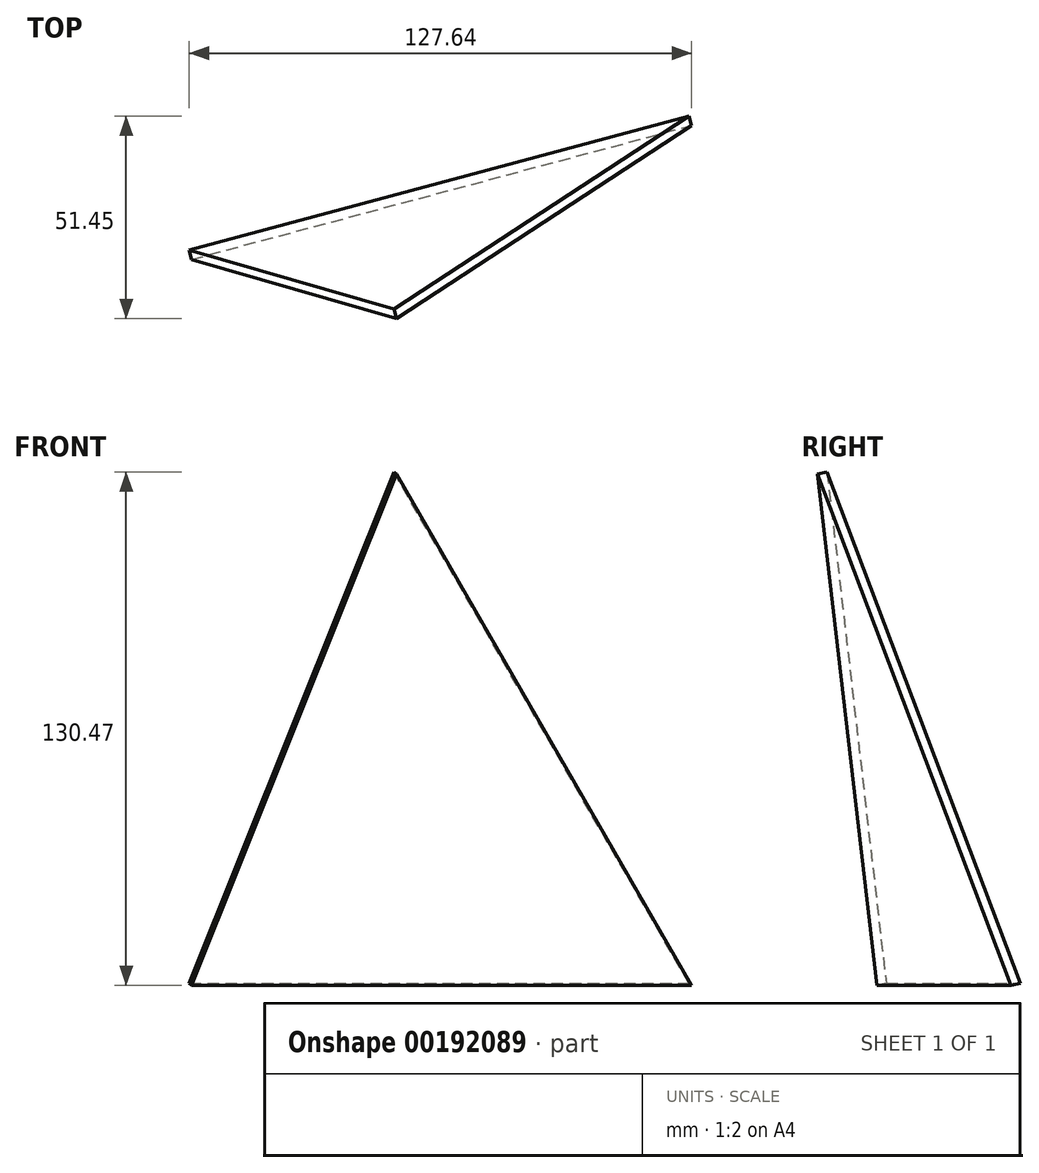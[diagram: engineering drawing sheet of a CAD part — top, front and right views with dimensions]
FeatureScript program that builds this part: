
annotation { "Feature Type Name" : "Feature", "Feature Type Description" : "" }
export const myFeature = defineFeature(function(context is Context, id is Id, definition is map)
    precondition{}
    {
        {
            var Q0;
            Q0=qCreatedBy(makeId("Top.planeOp"),FACE);
            var sketch = newSketch(context, id + "F0", { "sketchPlane" : qUnion([Q0])});
            skCircle(sketch, "E0.cCircle", {"center": v(0, -146.65) * mm, "radius": 73.32 * mm, "construction": true});
            skLineSegment(sketch, "E0.0", {"start": v(0, 0) * mm, "end": v(127, -219.97) * mm, "construction": true});
            skLineSegment(sketch, "E0.1", {"start": v(127, -219.97) * mm, "end": v(-127, -219.97) * mm, "construction": true});
            skLineSegment(sketch, "E0.2", {"start": v(-127, -219.97) * mm, "end": v(0, 0) * mm, "construction": true});
            skPoint(sketch, "E0.0.midPoint", {"position": v(63.5, -109.99) * mm});
            skLineSegment(sketch, "E1", {"start": v(0, 0) * mm, "end": v(-127, 219.97) * mm, "construction": true});
            skLineSegment(sketch, "E2", {"start": v(-127, 219.97) * mm, "end": v(127, 219.97) * mm, "construction": true});
            skLineSegment(sketch, "E3", {"start": v(127, 219.97) * mm, "end": v(0, 0) * mm, "construction": true});
            skArc(sketch, "E4", {"start": v(-127, -219.97) * mm, "mid": v(0, -254) * mm, "end": v(127, -219.97) * mm, "construction": true});
            skArc(sketch, "E5.trimOffspring", {"start": v(127, 219.97) * mm, "mid": v(65.74, 245.35) * mm, "end": v(0, 254) * mm, "construction": true});
            skArc(sketch, "E6", {"start": v(0, 254) * mm, "mid": v(-65.74, 245.35) * mm, "end": v(-127, 219.97) * mm, "construction": true});
            skLineSegment(sketch, "E7", {"start": v(-127, 219.97) * mm, "end": v(0, 254) * mm, "construction": true});
            skLineSegment(sketch, "E8", {"start": v(0, 254) * mm, "end": v(127, 219.97) * mm, "construction": true});
            skSolve(sketch);
        }
        {
            var Q0;
            Q0=qCreatedBy(makeId("Right.planeOp"),FACE);
            var sketch = newSketch(context, id + "F1", { "sketchPlane" : qUnion([Q0])});
            skLineSegment(sketch, "E9", {"start": v(0, 0) * mm, "end": v(-127, -219.97) * mm, "construction": true});
            skLineSegment(sketch, "E10", {"start": v(-127, -219.97) * mm, "end": v(127, -219.97) * mm, "construction": true});
            skLineSegment(sketch, "E11", {"start": v(127, -219.97) * mm, "end": v(0, 0) * mm, "construction": true});
            skLineSegment(sketch, "E12", {"start": v(-127, 219.97) * mm, "end": v(0, 0) * mm, "construction": true});
            skLineSegment(sketch, "E13", {"start": v(127, 219.97) * mm, "end": v(-127, 219.97) * mm, "construction": true});
            skLineSegment(sketch, "E14", {"start": v(0, 0) * mm, "end": v(127, 219.97) * mm, "construction": true});
            skArc(sketch, "E15", {"start": v(127, 219.97) * mm, "mid": v(0, 254) * mm, "end": v(-127, 219.97) * mm, "construction": true});
            skArc(sketch, "E16.trimOffspring", {"start": v(-127, -219.97) * mm, "mid": v(0, -254) * mm, "end": v(127, -219.97) * mm, "construction": true});
            skLineSegment(sketch, "E17", {"start": v(127, 219.97) * mm, "end": v(0, 254) * mm, "construction": true});
            skLineSegment(sketch, "E18", {"start": v(0, 254) * mm, "end": v(-127, 219.97) * mm, "construction": true});
            skLineSegment(sketch, "E19", {"start": v(127, -219.97) * mm, "end": v(0, -254) * mm, "construction": true});
            skLineSegment(sketch, "E20", {"start": v(0, -254) * mm, "end": v(-127, -219.97) * mm, "construction": true});
            skSolve(sketch);
        }
        {
            var Q0;
            Q0=qCreatedBy(makeId("Front.planeOp"),FACE);
            var sketch = newSketch(context, id + "F2", { "sketchPlane" : qUnion([Q0])});
            skLineSegment(sketch, "E21", {"start": v(-219.97, -127) * mm, "end": v(0, 0) * mm, "construction": true});
            skLineSegment(sketch, "E22", {"start": v(219.97, 127) * mm, "end": v(219.97, -127) * mm, "construction": true});
            skLineSegment(sketch, "E23", {"start": v(219.97, -127) * mm, "end": v(0, 0) * mm, "construction": true});
            skLineSegment(sketch, "E24", {"start": v(-219.97, 127) * mm, "end": v(-219.97, -127) * mm, "construction": true});
            skLineSegment(sketch, "E25", {"start": v(0, 0) * mm, "end": v(219.97, 127) * mm, "construction": true});
            skLineSegment(sketch, "E26", {"start": v(0, 0) * mm, "end": v(-219.97, 127) * mm, "construction": true});
            skArc(sketch, "E27", {"start": v(-219.97, 127) * mm, "mid": v(-254, 0) * mm, "end": v(-219.97, -127) * mm, "construction": true});
            skArc(sketch, "E28.trimOffspring", {"start": v(219.97, -127) * mm, "mid": v(254, 0) * mm, "end": v(219.97, 127) * mm, "construction": true});
            skArc(sketch, "E29", {"start": v(-219.97, 127) * mm, "mid": v(0, 254) * mm, "end": v(219.97, 127) * mm, "construction": true});
            skArc(sketch, "E30", {"start": v(-219.97, -127) * mm, "mid": v(0, -254) * mm, "end": v(219.97, -127) * mm, "construction": true});
            skLineSegment(sketch, "E31", {"start": v(219.97, 127) * mm, "end": v(254, 0) * mm, "construction": true});
            skLineSegment(sketch, "E32", {"start": v(254, 0) * mm, "end": v(219.97, -127) * mm, "construction": true});
            skLineSegment(sketch, "E33", {"start": v(-219.97, 127) * mm, "end": v(-254, 0) * mm, "construction": true});
            skLineSegment(sketch, "E34", {"start": v(-254, 0) * mm, "end": v(-219.97, -127) * mm, "construction": true});
            skSolve(sketch);
        }
        {
            var Q0;
            Q0=sQuery(id+"F0.wireOp",VERTEX,"E3.start");
            var Q1;
            Q1=sQuery(id+"F2.wireOp",VERTEX,"E23.start");
            var Q2;
            Q2=sQuery(id+"F1.wireOp",VERTEX,"E11.start");
            cPlane(context, id + "F3", {"entities" : qUnion([Q0, Q1, Q2]), "cplaneType" : CPlaneType.THREE_POINT, "offset" : 25.4 * mm, "width" : 152.4 * mm, "height" : 152.4 * mm});
        }
        {
            var Q0;
            Q0=sQuery(id+"F1.wireOp",VERTEX,"E14.end");
            var Q1;
            Q1=sQuery(id+"F0.wireOp",VERTEX,"E3.start");
            var Q2;
            Q2=sQuery(id+"F2.wireOp",VERTEX,"E25.end");
            cPlane(context, id + "F4", {"entities" : qUnion([Q0, Q1, Q2]), "cplaneType" : CPlaneType.THREE_POINT, "offset" : 25.4 * mm, "width" : 152.4 * mm, "height" : 152.4 * mm});
        }
        {
            var Q0;
            Q0=sQuery(id+"F1.wireOp",VERTEX,"E14.end");
            var Q1;
            Q1=sQuery(id+"F0.wireOp",VERTEX,"E2.start");
            var Q2;
            Q2=sQuery(id+"F2.wireOp",VERTEX,"E26.end");
            cPlane(context, id + "F5", {"entities" : qUnion([Q0, Q1, Q2]), "cplaneType" : CPlaneType.THREE_POINT, "offset" : 25.4 * mm, "width" : 152.4 * mm, "height" : 152.4 * mm});
        }
        {
            var Q0;
            Q0=sQuery(id+"F0.wireOp",VERTEX,"E2.start");
            var Q1;
            Q1=sQuery(id+"F2.wireOp",VERTEX,"E24.end");
            var Q2;
            Q2=sQuery(id+"F1.wireOp",VERTEX,"E11.start");
            cPlane(context, id + "F6", {"entities" : qUnion([Q0, Q1, Q2]), "cplaneType" : CPlaneType.THREE_POINT, "offset" : 25.4 * mm, "width" : 152.4 * mm, "height" : 152.4 * mm});
        }
        {
            var Q0;
            Q0=qCreatedBy(id+"F4.planeOp",FACE);
            var sketch = newSketch(context, id + "F7", { "sketchPlane" : qUnion([Q0])});
            skLineSegment(sketch, "E35", {"start": v(13.9, 155.54) * mm, "end": v(127.76, -89.8) * mm, "construction": true});
            skLineSegment(sketch, "E36", {"start": v(127.76, -89.8) * mm, "end": v(-141.65, -65.74) * mm, "construction": true});
            skLineSegment(sketch, "E37", {"start": v(-141.65, -65.74) * mm, "end": v(13.9, 155.54) * mm, "construction": true});
            skSolve(sketch);
        }
        {
            var Q0;
            Q0=qCreatedBy(id+"F5.planeOp",FACE);
            var sketch = newSketch(context, id + "F8", { "sketchPlane" : qUnion([Q0])});
            skLineSegment(sketch, "E38", {"start": v(-13.9, -155.54) * mm, "end": v(141.65, 65.74) * mm, "construction": true});
            skLineSegment(sketch, "E39", {"start": v(141.65, 65.74) * mm, "end": v(-127.76, 89.8) * mm, "construction": true});
            skLineSegment(sketch, "E40", {"start": v(-127.76, 89.8) * mm, "end": v(-13.9, -155.54) * mm, "construction": true});
            skSolve(sketch);
        }
        {
            var Q0;
            Q0=sQuery(id+"F1.wireOp",VERTEX,"E11.start");
            var Q1;
            Q1=sQuery(id+"F0.wireOp",VERTEX,"E2.start");
            var Q2;
            Q2=qCreatedBy(makeId("Origin.pointOp"),VERTEX);
            cPlane(context, id + "F9", {"entities" : qUnion([Q0, Q1, Q2]), "cplaneType" : CPlaneType.THREE_POINT, "offset" : 25.4 * mm, "width" : 152.4 * mm, "height" : 152.4 * mm});
        }
        {
            var Q0;
            Q0=sQuery(id+"F1.wireOp",VERTEX,"E11.start");
            var Q1;
            Q1=sQuery(id+"F2.wireOp",VERTEX,"E24.end");
            var Q2;
            Q2=qCreatedBy(makeId("Origin.pointOp"),VERTEX);
            cPlane(context, id + "F10", {"entities" : qUnion([Q0, Q1, Q2]), "cplaneType" : CPlaneType.THREE_POINT, "offset" : 25.4 * mm, "width" : 152.4 * mm, "height" : 152.4 * mm});
        }
        {
            var Q0;
            Q0=sQuery(id+"F2.wireOp",VERTEX,"E24.end");
            var Q1;
            Q1=sQuery(id+"F0.wireOp",VERTEX,"E2.start");
            var Q2;
            Q2=qCreatedBy(makeId("Origin.pointOp"),VERTEX);
            cPlane(context, id + "F11", {"entities" : qUnion([Q0, Q1, Q2]), "cplaneType" : CPlaneType.THREE_POINT, "offset" : 25.4 * mm, "width" : 152.4 * mm, "height" : 152.4 * mm});
        }
        {
            var Q0;
            Q0=qCreatedBy(id+"F9.planeOp",FACE);
            var sketch = newSketch(context, id + "F12", { "sketchPlane" : qUnion([Q0])});
            skLineSegment(sketch, "E41.0", {"start": v(0, 0) * mm, "end": v(-250.8, 40.16) * mm, "construction": true});
            skLineSegment(sketch, "E42.0", {"start": v(-144.8, -208.68) * mm, "end": v(0, 0) * mm, "construction": true});
            skLineSegment(sketch, "E43", {"start": v(-250.8, 40.16) * mm, "end": v(-144.8, -208.68) * mm, "construction": true});
            skArc(sketch, "E44.trimOffspring", {"start": v(-250.8, 40.16) * mm, "mid": v(-233.68, -99.54) * mm, "end": v(-144.8, -208.68) * mm, "construction": true});
            skLineSegment(sketch, "E45", {"start": v(-144.8, -208.68) * mm, "end": v(-233.68, -99.54) * mm, "construction": true});
            skLineSegment(sketch, "E46", {"start": v(-233.68, -99.54) * mm, "end": v(-250.8, 40.16) * mm, "construction": true});
            skSolve(sketch);
        }
        {
            var Q0;
            Q0=qCreatedBy(id+"F10.planeOp",FACE);
            var sketch = newSketch(context, id + "F13", { "sketchPlane" : qUnion([Q0])});
            skArc(sketch, "E47", {"start": v(-228.95, -109.99) * mm, "mid": v(-135.24, -215) * mm, "end": v(0, -254) * mm, "construction": true});
            skLineSegment(sketch, "E48.0", {"start": v(-228.95, -109.99) * mm, "end": v(0, 0) * mm, "construction": true});
            skLineSegment(sketch, "E48.1", {"start": v(0, -254) * mm, "end": v(0, 0) * mm, "construction": true});
            skLineSegment(sketch, "E49", {"start": v(-228.95, -109.99) * mm, "end": v(0, -254) * mm, "construction": true});
            skLineSegment(sketch, "E50", {"start": v(-228.95, -109.99) * mm, "end": v(-135.24, -215) * mm, "construction": true});
            skLineSegment(sketch, "E51", {"start": v(-135.24, -215) * mm, "end": v(0, -254) * mm, "construction": true});
            skSolve(sketch);
        }
        {
            var Q0;
            Q0=qCreatedBy(id+"F11.planeOp",FACE);
            var sketch = newSketch(context, id + "F14", { "sketchPlane" : qUnion([Q0])});
            skArc(sketch, "E52", {"start": v(-144.8, 208.68) * mm, "mid": v(-233.68, 99.54) * mm, "end": v(-250.8, -40.16) * mm, "construction": true});
            skLineSegment(sketch, "E53.1", {"start": v(0, 0) * mm, "end": v(-144.8, 208.68) * mm, "construction": true});
            skLineSegment(sketch, "E53.2", {"start": v(-250.8, -40.16) * mm, "end": v(0, 0) * mm, "construction": true});
            skLineSegment(sketch, "E54", {"start": v(-144.8, 208.68) * mm, "end": v(-250.8, -40.16) * mm, "construction": true});
            skLineSegment(sketch, "E55", {"start": v(-250.8, -40.16) * mm, "end": v(-233.68, 99.54) * mm, "construction": true});
            skLineSegment(sketch, "E56", {"start": v(-233.68, 99.54) * mm, "end": v(-144.8, 208.68) * mm, "construction": true});
            skSolve(sketch);
        }
        {
            var Q0;
            Q0=sQuery(id+"F2.wireOp",VERTEX,"E30.end");
            var Q1;
            Q1=qCreatedBy(makeId("Origin.pointOp"),VERTEX);
            var Q2;
            Q2=sQuery(id+"F1.wireOp",VERTEX,"E11.start");
            cPlane(context, id + "F15", {"entities" : qUnion([Q0, Q1, Q2]), "cplaneType" : CPlaneType.THREE_POINT, "offset" : 25.4 * mm, "width" : 152.4 * mm, "height" : 152.4 * mm});
        }
        {
            var Q0;
            Q0=qCreatedBy(makeId("Origin.pointOp"),VERTEX);
            var Q1;
            Q1=sQuery(id+"F2.wireOp",VERTEX,"E30.end");
            var Q2;
            Q2=sQuery(id+"F0.wireOp",VERTEX,"E3.start");
            cPlane(context, id + "F16", {"entities" : qUnion([Q0, Q1, Q2]), "cplaneType" : CPlaneType.THREE_POINT, "offset" : 25.4 * mm, "width" : 152.4 * mm, "height" : 152.4 * mm});
        }
        {
            var Q0;
            Q0=qCreatedBy(makeId("Origin.pointOp"),VERTEX);
            var Q1;
            Q1=sQuery(id+"F0.wireOp",VERTEX,"E3.start");
            var Q2;
            Q2=sQuery(id+"F1.wireOp",VERTEX,"E11.start");
            cPlane(context, id + "F17", {"entities" : qUnion([Q0, Q1, Q2]), "cplaneType" : CPlaneType.THREE_POINT, "offset" : 25.4 * mm, "width" : 152.4 * mm, "height" : 152.4 * mm});
        }
        {
            var Q0;
            Q0=qCreatedBy(makeId("Origin.pointOp"),VERTEX);
            var Q1;
            Q1=sQuery(id+"F0.wireOp",VERTEX,"E3.start");
            var Q2;
            Q2=sQuery(id+"F2.wireOp",VERTEX,"E25.end");
            cPlane(context, id + "F18", {"entities" : qUnion([Q0, Q1, Q2]), "cplaneType" : CPlaneType.THREE_POINT, "offset" : 25.4 * mm, "width" : 152.4 * mm, "height" : 152.4 * mm});
        }
        {
            var Q0;
            Q0=qCreatedBy(makeId("Origin.pointOp"),VERTEX);
            var Q1;
            Q1=sQuery(id+"F2.wireOp",VERTEX,"E25.end");
            var Q2;
            Q2=sQuery(id+"F1.wireOp",VERTEX,"E15.start");
            cPlane(context, id + "F19", {"entities" : qUnion([Q0, Q1, Q2]), "cplaneType" : CPlaneType.THREE_POINT, "offset" : 25.4 * mm, "width" : 152.4 * mm, "height" : 152.4 * mm});
        }
        {
            var Q0;
            Q0=qCreatedBy(makeId("Origin.pointOp"),VERTEX);
            var Q1;
            Q1=sQuery(id+"F1.wireOp",VERTEX,"E15.start");
            var Q2;
            Q2=sQuery(id+"F0.wireOp",VERTEX,"E3.start");
            cPlane(context, id + "F20", {"entities" : qUnion([Q0, Q1, Q2]), "cplaneType" : CPlaneType.THREE_POINT, "offset" : 25.4 * mm, "width" : 152.4 * mm, "height" : 152.4 * mm});
        }
        {
            var Q0;
            Q0=qCreatedBy(makeId("Origin.pointOp"),VERTEX);
            var Q1;
            Q1=sQuery(id+"F0.wireOp",VERTEX,"E2.start");
            var Q2;
            Q2=sQuery(id+"F2.wireOp",VERTEX,"E27.start");
            cPlane(context, id + "F21", {"entities" : qUnion([Q0, Q1, Q2]), "cplaneType" : CPlaneType.THREE_POINT, "offset" : 25.4 * mm, "width" : 152.4 * mm, "height" : 152.4 * mm});
        }
        {
            var Q0;
            Q0=qCreatedBy(makeId("Origin.pointOp"),VERTEX);
            var Q1;
            Q1=sQuery(id+"F0.wireOp",VERTEX,"E2.start");
            var Q2;
            Q2=sQuery(id+"F1.wireOp",VERTEX,"E15.start");
            cPlane(context, id + "F22", {"entities" : qUnion([Q0, Q1, Q2]), "cplaneType" : CPlaneType.THREE_POINT, "offset" : 25.4 * mm, "width" : 152.4 * mm, "height" : 152.4 * mm});
        }
        {
            var Q0;
            Q0=qCreatedBy(makeId("Origin.pointOp"),VERTEX);
            var Q1;
            Q1=sQuery(id+"F2.wireOp",VERTEX,"E27.start");
            var Q2;
            Q2=sQuery(id+"F1.wireOp",VERTEX,"E15.start");
            cPlane(context, id + "F23", {"entities" : qUnion([Q0, Q1, Q2]), "cplaneType" : CPlaneType.THREE_POINT, "offset" : 25.4 * mm, "width" : 152.4 * mm, "height" : 152.4 * mm});
        }
        {
            var Q0;
            Q0=qCreatedBy(id+"F15.planeOp",FACE);
            var sketch = newSketch(context, id + "F24", { "sketchPlane" : qUnion([Q0])});
            skArc(sketch, "E57", {"start": v(-228.95, -109.99) * mm, "mid": v(-135.24, -215) * mm, "end": v(0, -254) * mm, "construction": true});
            skLineSegment(sketch, "E58.0", {"start": v(-228.95, -109.99) * mm, "end": v(0, 0) * mm, "construction": true});
            skLineSegment(sketch, "E58.1", {"start": v(0, -254) * mm, "end": v(0, 0) * mm, "construction": true});
            skLineSegment(sketch, "E59", {"start": v(0, -254) * mm, "end": v(-228.95, -109.99) * mm, "construction": true});
            skLineSegment(sketch, "E60", {"start": v(-228.95, -109.99) * mm, "end": v(-135.24, -215) * mm, "construction": true});
            skLineSegment(sketch, "E61", {"start": v(-135.24, -215) * mm, "end": v(0, -254) * mm, "construction": true});
            skSolve(sketch);
        }
        {
            var Q0;
            Q0=qCreatedBy(id+"F16.planeOp",FACE);
            var sketch = newSketch(context, id + "F25", { "sketchPlane" : qUnion([Q0])});
            skArc(sketch, "E62", {"start": v(144.8, -208.68) * mm, "mid": v(233.68, -99.54) * mm, "end": v(250.8, 40.16) * mm, "construction": true});
            skLineSegment(sketch, "E63.0", {"start": v(144.8, -208.68) * mm, "end": v(0, 0) * mm, "construction": true});
            skLineSegment(sketch, "E63.1", {"start": v(250.8, 40.16) * mm, "end": v(0, 0) * mm, "construction": true});
            skLineSegment(sketch, "E64", {"start": v(144.8, -208.68) * mm, "end": v(250.8, 40.16) * mm, "construction": true});
            skLineSegment(sketch, "E65", {"start": v(144.8, -208.68) * mm, "end": v(233.68, -99.54) * mm, "construction": true});
            skLineSegment(sketch, "E66", {"start": v(233.68, -99.54) * mm, "end": v(250.8, 40.16) * mm, "construction": true});
            skSolve(sketch);
        }
        {
            var Q0;
            Q0=qCreatedBy(id+"F17.planeOp",FACE);
            var sketch = newSketch(context, id + "F26", { "sketchPlane" : qUnion([Q0])});
            skArc(sketch, "E67", {"start": v(144.8, -208.68) * mm, "mid": v(233.68, -99.54) * mm, "end": v(250.8, 40.16) * mm, "construction": true});
            skLineSegment(sketch, "E68.0", {"start": v(250.8, 40.16) * mm, "end": v(0, 0) * mm, "construction": true});
            skLineSegment(sketch, "E68.1", {"start": v(144.8, -208.68) * mm, "end": v(0, 0) * mm, "construction": true});
            skLineSegment(sketch, "E69", {"start": v(250.8, 40.16) * mm, "end": v(144.8, -208.68) * mm, "construction": true});
            skLineSegment(sketch, "E70", {"start": v(250.8, 40.16) * mm, "end": v(233.68, -99.54) * mm, "construction": true});
            skLineSegment(sketch, "E71", {"start": v(233.68, -99.54) * mm, "end": v(144.8, -208.68) * mm, "construction": true});
            skSolve(sketch);
        }
        {
            var Q0;
            Q0=qCreatedBy(id+"F18.planeOp",FACE);
            var sketch = newSketch(context, id + "F27", { "sketchPlane" : qUnion([Q0])});
            skArc(sketch, "E72", {"start": v(250.8, -40.16) * mm, "mid": v(233.68, 99.54) * mm, "end": v(144.8, 208.68) * mm, "construction": true});
            skLineSegment(sketch, "E73.0", {"start": v(144.8, 208.68) * mm, "end": v(0, 0) * mm, "construction": true});
            skLineSegment(sketch, "E73.1", {"start": v(0, 0) * mm, "end": v(250.8, -40.16) * mm, "construction": true});
            skLineSegment(sketch, "E74", {"start": v(144.8, 208.68) * mm, "end": v(250.8, -40.16) * mm, "construction": true});
            skLineSegment(sketch, "E75", {"start": v(144.8, 208.68) * mm, "end": v(233.68, 99.54) * mm, "construction": true});
            skLineSegment(sketch, "E76", {"start": v(233.68, 99.54) * mm, "end": v(250.8, -40.16) * mm, "construction": true});
            skSolve(sketch);
        }
        {
            var Q0;
            Q0=qCreatedBy(id+"F19.planeOp",FACE);
            var sketch = newSketch(context, id + "F28", { "sketchPlane" : qUnion([Q0])});
            skArc(sketch, "E77", {"start": v(0, 254) * mm, "mid": v(-135.24, 215) * mm, "end": v(-228.95, 109.99) * mm, "construction": true});
            skLineSegment(sketch, "E78.0", {"start": v(0, 0) * mm, "end": v(0, 254) * mm, "construction": true});
            skLineSegment(sketch, "E78.1", {"start": v(0, 0) * mm, "end": v(-228.95, 109.99) * mm, "construction": true});
            skLineSegment(sketch, "E79", {"start": v(0, 254) * mm, "end": v(-228.95, 109.99) * mm, "construction": true});
            skLineSegment(sketch, "E80", {"start": v(0, 254) * mm, "end": v(-135.24, 215) * mm, "construction": true});
            skLineSegment(sketch, "E81", {"start": v(-135.24, 215) * mm, "end": v(-228.95, 109.99) * mm, "construction": true});
            skSolve(sketch);
        }
        {
            var Q0;
            Q0=qCreatedBy(id+"F20.planeOp",FACE);
            var sketch = newSketch(context, id + "F29", { "sketchPlane" : qUnion([Q0])});
            skArc(sketch, "E82", {"start": v(250.8, -40.16) * mm, "mid": v(233.68, 99.54) * mm, "end": v(144.8, 208.68) * mm, "construction": true});
            skLineSegment(sketch, "E83.0", {"start": v(250.8, -40.16) * mm, "end": v(0, 0) * mm, "construction": true});
            skLineSegment(sketch, "E83.1", {"start": v(0, 0) * mm, "end": v(144.8, 208.68) * mm, "construction": true});
            skLineSegment(sketch, "E84", {"start": v(250.8, -40.16) * mm, "end": v(144.8, 208.68) * mm, "construction": true});
            skLineSegment(sketch, "E85", {"start": v(144.8, 208.68) * mm, "end": v(233.68, 99.54) * mm, "construction": true});
            skLineSegment(sketch, "E86", {"start": v(233.68, 99.54) * mm, "end": v(250.8, -40.16) * mm, "construction": true});
            skSolve(sketch);
        }
        {
            var Q0;
            Q0=qCreatedBy(id+"F21.planeOp",FACE);
            var sketch = newSketch(context, id + "F30", { "sketchPlane" : qUnion([Q0])});
            skArc(sketch, "E87", {"start": v(-250.8, 40.16) * mm, "mid": v(-233.68, -99.54) * mm, "end": v(-144.8, -208.68) * mm, "construction": true});
            skLineSegment(sketch, "E88.0", {"start": v(0, 0) * mm, "end": v(-144.8, -208.68) * mm, "construction": true});
            skLineSegment(sketch, "E88.1", {"start": v(0, 0) * mm, "end": v(-250.8, 40.16) * mm, "construction": true});
            skLineSegment(sketch, "E89", {"start": v(-144.8, -208.68) * mm, "end": v(-250.8, 40.16) * mm, "construction": true});
            skLineSegment(sketch, "E90", {"start": v(-250.8, 40.16) * mm, "end": v(-233.68, -99.54) * mm, "construction": true});
            skLineSegment(sketch, "E91", {"start": v(-233.68, -99.54) * mm, "end": v(-144.8, -208.68) * mm, "construction": true});
            skSolve(sketch);
        }
        {
            var Q0;
            Q0=qCreatedBy(id+"F22.planeOp",FACE);
            var sketch = newSketch(context, id + "F31", { "sketchPlane" : qUnion([Q0])});
            skArc(sketch, "E92", {"start": v(-144.8, 208.68) * mm, "mid": v(-233.68, 99.54) * mm, "end": v(-250.8, -40.16) * mm, "construction": true});
            skLineSegment(sketch, "E93.1", {"start": v(0, 0) * mm, "end": v(-250.8, -40.16) * mm, "construction": true});
            skLineSegment(sketch, "E93.2", {"start": v(0, 0) * mm, "end": v(-144.8, 208.68) * mm, "construction": true});
            skLineSegment(sketch, "E94", {"start": v(-250.8, -40.16) * mm, "end": v(-144.8, 208.68) * mm, "construction": true});
            skLineSegment(sketch, "E95", {"start": v(-144.8, 208.68) * mm, "end": v(-233.68, 99.54) * mm, "construction": true});
            skLineSegment(sketch, "E96", {"start": v(-233.68, 99.54) * mm, "end": v(-250.8, -40.16) * mm, "construction": true});
            skSolve(sketch);
        }
        {
            var Q0;
            Q0=qCreatedBy(id+"F23.planeOp",FACE);
            var sketch = newSketch(context, id + "F32", { "sketchPlane" : qUnion([Q0])});
            skArc(sketch, "E97", {"start": v(0, 254) * mm, "mid": v(-135.24, 215) * mm, "end": v(-228.95, 109.99) * mm, "construction": true});
            skLineSegment(sketch, "E98.0", {"start": v(0, 0) * mm, "end": v(-228.95, 109.99) * mm, "construction": true});
            skLineSegment(sketch, "E98.1", {"start": v(0, 0) * mm, "end": v(0, 254) * mm, "construction": true});
            skLineSegment(sketch, "E99", {"start": v(-228.95, 109.99) * mm, "end": v(0, 254) * mm, "construction": true});
            skLineSegment(sketch, "E100", {"start": v(0, 254) * mm, "end": v(-135.24, 215) * mm, "construction": true});
            skLineSegment(sketch, "E101", {"start": v(-135.24, 215) * mm, "end": v(-228.95, 109.99) * mm, "construction": true});
            skSolve(sketch);
        }
        {
            var Q0;
            Q0=sQuery(id+"F0.wireOp",VERTEX,"E5.trimOffspring.end");
            var Q1;
            Q1=sQuery(id+"F26.wireOp",VERTEX,"E71.start");
            var Q2;
            Q2=sQuery(id+"F12.wireOp",VERTEX,"E46.start");
            cPlane(context, id + "F33", {"entities" : qUnion([Q0, Q1, Q2]), "cplaneType" : CPlaneType.THREE_POINT, "offset" : 25.4 * mm, "width" : 152.4 * mm, "height" : 152.4 * mm});
        }
        {
            var Q0;
            Q0=sQuery(id+"F31.wireOp",VERTEX,"E96.start");
            var Q1;
            Q1=sQuery(id+"F0.wireOp",VERTEX,"E6.start");
            var Q2;
            Q2=sQuery(id+"F29.wireOp",VERTEX,"E86.start");
            cPlane(context, id + "F34", {"entities" : qUnion([Q0, Q1, Q2]), "cplaneType" : CPlaneType.THREE_POINT, "offset" : 25.4 * mm, "width" : 152.4 * mm, "height" : 152.4 * mm});
        }
        {
            var Q0;
            Q0=sQuery(id+"F31.wireOp",VERTEX,"E96.start");
            var Q1;
            Q1=sQuery(id+"F30.wireOp",VERTEX,"E91.start");
            var Q2;
            Q2=sQuery(id+"F32.wireOp",VERTEX,"E101.start");
            cPlane(context, id + "F35", {"entities" : qUnion([Q0, Q1, Q2]), "cplaneType" : CPlaneType.THREE_POINT, "offset" : 25.4 * mm, "width" : 152.4 * mm, "height" : 152.4 * mm});
        }
        {
            var Q0;
            Q0=sQuery(id+"F14.wireOp",VERTEX,"E56.start");
            var Q1;
            Q1=sQuery(id+"F12.wireOp",VERTEX,"E46.start");
            var Q2;
            Q2=sQuery(id+"F13.wireOp",VERTEX,"E51.start");
            cPlane(context, id + "F36", {"entities" : qUnion([Q0, Q1, Q2]), "cplaneType" : CPlaneType.THREE_POINT, "offset" : 25.4 * mm, "width" : 152.4 * mm, "height" : 152.4 * mm});
        }
        {
            var Q0;
            Q0=sQuery(id+"F26.wireOp",VERTEX,"E71.start");
            var Q1;
            Q1=sQuery(id+"F25.wireOp",VERTEX,"E66.start");
            var Q2;
            Q2=sQuery(id+"F24.wireOp",VERTEX,"E61.start");
            cPlane(context, id + "F37", {"entities" : qUnion([Q0, Q1, Q2]), "cplaneType" : CPlaneType.THREE_POINT, "offset" : 25.4 * mm, "width" : 152.4 * mm, "height" : 152.4 * mm});
        }
        {
            var Q0;
            Q0=sQuery(id+"F28.wireOp",EDGE,"E77");
            cPoint(context, id + "F38", {"entities" : qUnion([Q0]), "parameter" : 0.5});
        }
        {
            var Q0;
            Q0=sQuery(id+"F27.wireOp",EDGE,"E72");
            cPoint(context, id + "F39", {"entities" : qUnion([Q0]), "parameter" : 0.5});
        }
        {
            var Q0;
            Q0=sQuery(id+"F29.wireOp",VERTEX,"E86.start");
            var Q1;
            Q1 = qCreatedBy(id + "F38" ,VERTEX);
            var Q2;
            Q2 = qCreatedBy(id + "F39" ,VERTEX);
            cPlane(context, id + "F40", {"entities" : qUnion([Q0, Q1, Q2]), "cplaneType" : CPlaneType.THREE_POINT, "offset" : 25.4 * mm, "width" : 152.4 * mm, "height" : 152.4 * mm});
        }
        {
            var Q0;
            Q0=sQuery(id+"F2.wireOp",VERTEX,"E32.start");
            var Q1;
            Q1=sQuery(id+"F27.wireOp",VERTEX,"E76.start");
            var Q2;
            Q2=sQuery(id+"F25.wireOp",VERTEX,"E66.start");
            cPlane(context, id + "F41", {"entities" : qUnion([Q0, Q1, Q2]), "cplaneType" : CPlaneType.THREE_POINT, "offset" : 25.4 * mm, "width" : 152.4 * mm, "height" : 152.4 * mm});
        }
        {
            var Q0;
            Q0=sQuery(id+"F30.wireOp",EDGE,"E87");
            cPoint(context, id + "F42", {"entities" : qUnion([Q0]), "parameter" : 0.5});
        }
        {
            var Q0;
            Q0=sQuery(id+"F14.wireOp",VERTEX,"E56.start");
            var Q1;
            Q1 = qCreatedBy(id + "F42" ,VERTEX);
            var Q2;
            Q2=sQuery(id+"F2.wireOp",VERTEX,"E34.start");
            cPlane(context, id + "F43", {"entities" : qUnion([Q0, Q1, Q2]), "cplaneType" : CPlaneType.THREE_POINT, "offset" : 25.4 * mm, "width" : 152.4 * mm, "height" : 152.4 * mm});
        }
        {
            var Q0;
            Q0=qCreatedBy(id+"F33.planeOp",FACE);
            var sketch = newSketch(context, id + "F44", { "sketchPlane" : qUnion([Q0])});
            skPoint(sketch, "E102.0", {"position": v(-75.02, -49.18) * mm});
            skPoint(sketch, "E102.1", {"position": v(75.02, -49.18) * mm});
            skPoint(sketch, "E102.2", {"position": v(0, 89.7) * mm});
            skLineSegment(sketch, "E103", {"start": v(-75.02, -49.18) * mm, "end": v(0, 89.7) * mm, "construction": true});
            skLineSegment(sketch, "E104", {"start": v(75.02, -49.18) * mm, "end": v(-75.02, -49.18) * mm, "construction": true});
            skLineSegment(sketch, "E105", {"start": v(75.02, -49.18) * mm, "end": v(0, 89.7) * mm, "construction": true});
            skSolve(sketch);
        }
        {
            var Q0;
            Q0=qCreatedBy(id+"F34.planeOp",FACE);
            var sketch = newSketch(context, id + "F45", { "sketchPlane" : qUnion([Q0])});
            skPoint(sketch, "E106.0", {"position": v(-75.02, 49.18) * mm});
            skPoint(sketch, "E106.1", {"position": v(0, -89.7) * mm});
            skPoint(sketch, "E106.2", {"position": v(75.02, 49.18) * mm});
            skLineSegment(sketch, "E107", {"start": v(-75.02, 49.18) * mm, "end": v(75.02, 49.18) * mm, "construction": true});
            skLineSegment(sketch, "E108", {"start": v(0, -89.7) * mm, "end": v(-75.02, 49.18) * mm, "construction": true});
            skLineSegment(sketch, "E109", {"start": v(0, -89.7) * mm, "end": v(75.02, 49.18) * mm, "construction": true});
            skSolve(sketch);
        }
        {
            var Q0;
            Q0=qCreatedBy(id+"F35.planeOp",FACE);
            var sketch = newSketch(context, id + "F46", { "sketchPlane" : qUnion([Q0])});
            skPoint(sketch, "E110.0", {"position": v(83.67, 38.83) * mm});
            skPoint(sketch, "E110.1", {"position": v(-75.47, 53.05) * mm});
            skPoint(sketch, "E110.2", {"position": v(-8.2, -91.88) * mm});
            skLineSegment(sketch, "E111", {"start": v(83.67, 38.83) * mm, "end": v(-8.2, -91.88) * mm, "construction": true});
            skLineSegment(sketch, "E112", {"start": v(-8.2, -91.88) * mm, "end": v(-75.47, 53.05) * mm, "construction": true});
            skLineSegment(sketch, "E113", {"start": v(83.67, 38.83) * mm, "end": v(-75.47, 53.05) * mm, "construction": true});
            skSolve(sketch);
        }
        {
            var Q0;
            Q0=qCreatedBy(id+"F37.planeOp",FACE);
            var sketch = newSketch(context, id + "F47", { "sketchPlane" : qUnion([Q0])});
            skPoint(sketch, "E114.0", {"position": v(83.67, 38.83) * mm});
            skPoint(sketch, "E114.1", {"position": v(-8.2, -91.88) * mm});
            skPoint(sketch, "E114.2", {"position": v(-75.47, 53.05) * mm});
            skLineSegment(sketch, "E115", {"start": v(-8.2, -91.88) * mm, "end": v(83.67, 38.83) * mm, "construction": true});
            skLineSegment(sketch, "E116", {"start": v(83.67, 38.83) * mm, "end": v(-75.47, 53.05) * mm, "construction": true});
            skLineSegment(sketch, "E117", {"start": v(-75.47, 53.05) * mm, "end": v(-8.2, -91.88) * mm, "construction": true});
            skSolve(sketch);
        }
        {
            var Q0;
            Q0=qCreatedBy(id+"F40.planeOp",FACE);
            var sketch = newSketch(context, id + "F48", { "sketchPlane" : qUnion([Q0])});
            skPoint(sketch, "E118.0", {"position": v(8.2, -91.88) * mm});
            skPoint(sketch, "E118.1", {"position": v(75.47, 53.05) * mm});
            skPoint(sketch, "E118.2", {"position": v(-83.67, 38.83) * mm});
            skLineSegment(sketch, "E119", {"start": v(8.2, -91.88) * mm, "end": v(75.47, 53.05) * mm, "construction": true});
            skLineSegment(sketch, "E120", {"start": v(75.47, 53.05) * mm, "end": v(-83.67, 38.83) * mm, "construction": true});
            skLineSegment(sketch, "E121", {"start": v(-83.67, 38.83) * mm, "end": v(8.2, -91.88) * mm, "construction": true});
            skSolve(sketch);
        }
        {
            var Q0;
            Q0=sQuery(id+"F31.wireOp",EDGE,"E92");
            cPoint(context, id + "F49", {"entities" : qUnion([Q0]), "parameter" : 0.5});
        }
        {
            var Q0;
            Q0=sQuery(id+"F0.wireOp",VERTEX,"E7.start");
            var Q1;
            Q1 = qCreatedBy(id + "F49" ,VERTEX);
            var Q2;
            Q2=sQuery(id+"F45.wireOp",VERTEX,"E106.1");
            cPlane(context, id + "F50", {"entities" : qUnion([Q0, Q1, Q2]), "cplaneType" : CPlaneType.THREE_POINT, "offset" : 25.4 * mm, "width" : 152.4 * mm, "height" : 152.4 * mm});
        }
        {
            var Q0;
            Q0=qCreatedBy(id+"F50.planeOp",FACE);
            var sketch = newSketch(context, id + "F51", { "sketchPlane" : qUnion([Q0])});
            skLineSegment(sketch, "E122.0", {"start": v(-68.54, -47.83) * mm, "end": v(62.73, -55.23) * mm});
            skLineSegment(sketch, "E122.1", {"start": v(62.73, -55.23) * mm, "end": v(-14.8, 82.26) * mm});
            skLineSegment(sketch, "E122.2", {"start": v(-14.8, 82.26) * mm, "end": v(-68.54, -47.83) * mm});
            skSolve(sketch);
        }
        {
            var Q0;
            Q0=makeQuery(id+"F51.imprint","IMPRINT",FACE,{"disambiguationData":[TD([[makeQuery(id+"F51.imprint","IMPRINT",EDGE,{"derivedFrom":sQuery(id+"F51.wireOp",EDGE,"E122.0")}),1.0]])]});
            extrude(context, id + "F52", {"entities" : qUnion([Q0]), "oppositeDirection" : true, "depth" : 2.54 * mm});
        }
    });
